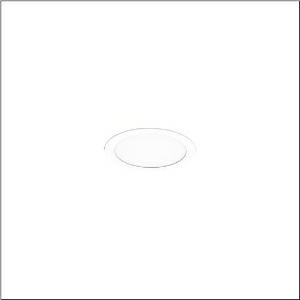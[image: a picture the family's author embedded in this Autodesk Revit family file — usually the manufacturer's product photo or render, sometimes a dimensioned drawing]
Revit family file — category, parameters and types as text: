
# Revit family: lunis_21_m_51db16ec91c
name_source: partatom
category: Lighting Fixtures
units: mm (PartAtom-declared; Revit-internal decimal feet)

## family parameters
Cut with Voids When Loaded = No
Host = Face
Light Source = No
Part Type = Normal
Room Calculation Point = No
Round Connector Dimension = Use Diameter
Shared = No

## types (1)
- --- (1 x LED, 3150 lm, 25.5 W, 6500K)
    Apparent Load = 26 VA
    CIE Flux Codes = 50 80 96 100 100
    Color Rendering = 80
    Color Temperature = 6500K
    Default Elevation = 1800 mm
    Description = Lunis 21 M, downlight, light control with lens, of PMMA, optical cover: cover panel, of PC, opal, light emission: direct distribution, LED rated luminous flux: 1.460lm, light colour: 830/840/865, with terminal, 5-pole, mains connection: 220..240V, AC/DC, 0/50..60Hz, housing, round, of diecast aluminium, traffic white (RAL 9016), diameter: 115mm, clamping range: 1..40mm, protection rating (complete): IP20, protection rating (on room side): IP54, insulation class (complete): insulation class II (safety insulation), certification: CE, impact resistance: IK03, packaging unit: 1 piece
    Height = 0 mm  [stored 0 ft]
    Lamp = 1 x LED
    Lamp Light Flux = 3150 lm
    Lamp Power = 25.5 W
    Lamp count = 1
    Length = 115 mm
    Luminous efficacy = 124 lm/W
    Manufacturer = Siteco
    ModVariant = No
    Model = 51DB16EC91C
    Mounting Place = Ceiling
    Mounting Type = Recessed
    Number of Poles = 1
    OnlyDefault = Yes
    Power Factor = 1
    Product Name = Lunis 21 M
    Product group = downlight
    ProductGroupID = 401
    Protection Class = Protection class II
    Protection Degree = IP 20
    RLX_Detail_Level = 1
    RLX_Emergency_Light_Flux = 0 lm
    RLX_Emergency_Type = 0
    RLX_Emergency_Type_DB = No
    RlxData = <blob elided: 13465 chars, md5=e73e1dd3>
    Socket = socket
    Standby Power = 0 W
    System Light Flux = 3150 lm
    System Power = 26 W
    Type Comments = individual setting: colour temperature 6500K, luminous flux: 100 % | (ON | ON | OFF | OFF) | 700 mA
    Type Image = l_1290848.jpg
    URL = http://relux.com
    VarID = @adj_034365
    Voltage = 0 V
    Weight = 0.00 kg
    Width = 0 mm  [stored 0 ft]

note: [stored X ft] marks values corroborated as IEEE doubles in the binary element streams (Revit-internal decimal feet)

## geometry (parser evidence)
native form markers: Sweep x8
no freeform markers — native parametric forms only
